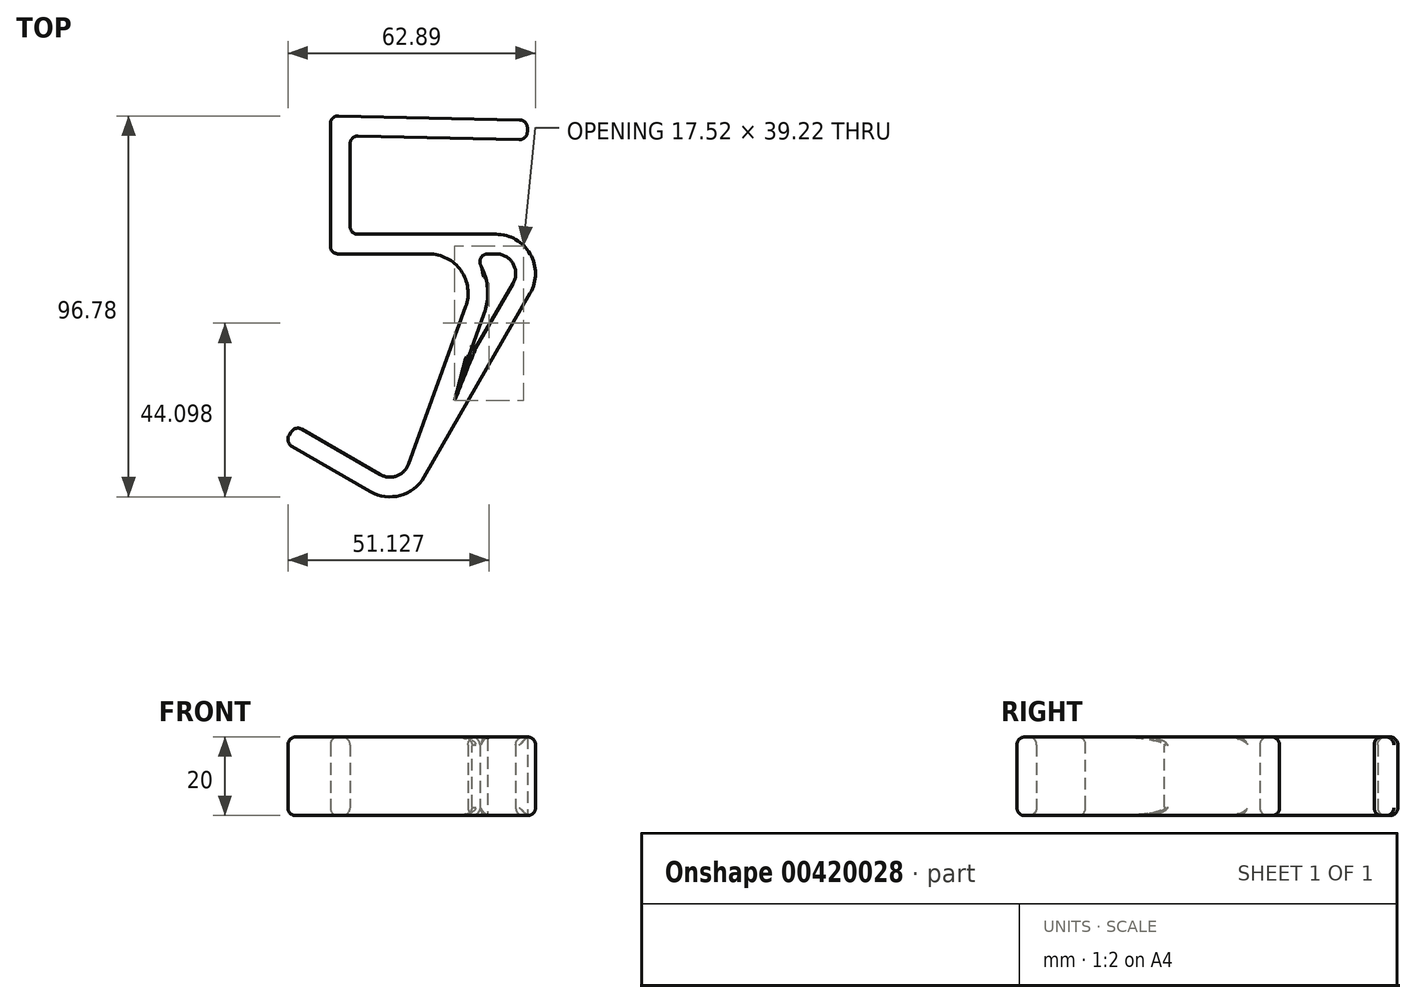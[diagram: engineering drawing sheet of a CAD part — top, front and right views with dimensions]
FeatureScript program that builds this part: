
annotation { "Feature Type Name" : "Feature", "Feature Type Description" : "" }
export const myFeature = defineFeature(function(context is Context, id is Id, definition is map)
    precondition{}
    {
        {
            var Q0;
            Q0=qCreatedBy(makeId("Top.planeOp"),FACE);
            var sketch = newSketch(context, id + "F0", { "sketchPlane" : qUnion([Q0])});
            skLineSegment(sketch, "E0.top", {"start": v(14.6, -12.5) * mm, "end": v(-22.5, -12.5) * mm});
            skLineSegment(sketch, "E0.right", {"start": v(-22.5, 12.5) * mm, "end": v(-22.5, -12.5) * mm});
            skPoint(sketch, "E0.middle", {"position": v(0, 0) * mm});
            skLineSegment(sketch, "E1", {"start": v(-22.5, 12.5) * mm, "end": v(22.5, 11.5) * mm});
            skLineSegment(sketch, "E2", {"start": v(6.9, -30.92) * mm, "end": v(-7.66, -70.92) * mm});
            skLineSegment(sketch, "E3", {"start": v(-14.86, -73.54) * mm, "end": v(-36.51, -61.04) * mm});
            skLineSegment(sketch, "E4.0", {"start": v(-27.5, 17.61) * mm, "end": v(22.61, 16.5) * mm});
            skLineSegment(sketch, "E4.1", {"start": v(-27.5, 17.61) * mm, "end": v(-27.5, -17.5) * mm});
            skLineSegment(sketch, "E4.2", {"start": v(-2.5, -17.5) * mm, "end": v(-27.5, -17.5) * mm});
            skPoint(sketch, "E5.visualSharp", {"position": v(-9.7, -76.52) * mm});
            skArc(sketch, "E5.filletArc", {"start": v(-14.86, -73.54) * mm, "mid": v(-10.65, -73.9) * mm, "end": v(-7.66, -70.92) * mm});
            skArc(sketch, "E6.filletArc", {"start": v(6.9, -30.92) * mm, "mid": v(5.7, -21.76) * mm, "end": v(-2.5, -17.5) * mm});
            skLineSegment(sketch, "E7.0", {"start": v(-17.36, -77.87) * mm, "end": v(-39.01, -65.37) * mm});
            skArc(sketch, "E7.1", {"start": v(-17.36, -77.87) * mm, "mid": v(-9.77, -78.87) * mm, "end": v(-3.7, -74.21) * mm});
            skLineSegment(sketch, "E7.2", {"start": v(11.6, -32.63) * mm, "end": v(6.59, -46.4) * mm});
            skArc(sketch, "E7.3", {"start": v(11.6, -32.63) * mm, "mid": v(12.23, -24.66) * mm, "end": v(8.68, -17.5) * mm});
            skLineSegment(sketch, "E8", {"start": v(-3.7, -74.21) * mm, "end": v(23.27, -27.5) * mm});
            skArc(sketch, "E9.filletArc", {"start": v(23.27, -27.5) * mm, "mid": v(23.27, -17.5) * mm, "end": v(14.6, -12.5) * mm});
            skLineSegment(sketch, "E10.0", {"start": v(14.6, -17.5) * mm, "end": v(-22.5, -17.5) * mm});
            skArc(sketch, "E10.1", {"start": v(18.94, -25) * mm, "mid": v(18.94, -20) * mm, "end": v(14.6, -17.5) * mm});
            skLineSegment(sketch, "E10.2", {"start": v(6.59, -46.4) * mm, "end": v(18.94, -25) * mm});
            skArc(sketch, "E11", {"start": v(8.68, -17.5) * mm, "mid": v(3.62, -13.8) * mm, "end": v(-2.5, -12.5) * mm, "construction": true});
            skLineSegment(sketch, "E12", {"start": v(22.61, 16.5) * mm, "end": v(22.5, 11.5) * mm});
            skLineSegment(sketch, "E13", {"start": v(-39.01, -65.37) * mm, "end": v(-36.51, -61.04) * mm});
            skSolve(sketch);
        }
        {
            var Q0;
            Q0=qSketchRegion(id+"F0",true);
            var Q1;
            Q1=makeQuery(id+"F0.imprint","IMPRINT",FACE,{"disambiguationData":[TD([[makeQuery(id+"F0.imprint","IMPRINT",EDGE,{"derivedFrom":sQuery(id+"F0.wireOp",EDGE,"E0.top")}),1.0]])]});
            extrude(context, id + "F1", {"entities" : qUnion([Q0, Q1]), "depth" : 20 * mm});
        }
        {
            var Q0;
            Q0=makeQuery(id+"F1.opExtrude","SWEPT_FACE",FACE,{"disambiguationData":[OSD([sQuery(id+"F0.wireOp",EDGE,"E4.1")])]});
            var Q1;
            Q1=makeQuery(id+"F1.opExtrude","SWEPT_FACE",FACE,{"disambiguationData":[OSD([sQuery(id+"F0.wireOp",EDGE,"E4.2"),sQuery(id+"F0.wireOp",EDGE,"E10.0")])]});
            var Q2;
            Q2=makeQuery(id+"F1.opExtrude","SWEPT_FACE",FACE,{"disambiguationData":[OSD([sQuery(id+"F0.wireOp",EDGE,"E4.0")])]});
            fillet(context, id + "F2", {"entities" : qUnion([Q0, Q1, Q2]), "radius" : 2 * mm, "tangentPropagation" : true, "allowEdgeOverflow" : false});
        }
        {
            var Q0;
            Q0=makeQuery(id+"F1.opExtrude","SWEPT_FACE",FACE,{"disambiguationData":[OSD([sQuery(id+"F0.wireOp",EDGE,"E8")])]});
            fillet(context, id + "F3", {"entities" : qUnion([Q0]), "radius" : 2 * mm, "tangentPropagation" : true, "allowEdgeOverflow" : false});
        }
        {
            var Q0;
            Q0=makeQuery(id+"F1.opExtrude","SWEPT_FACE",FACE,{"disambiguationData":[OSD([sQuery(id+"F0.wireOp",EDGE,"E1")])]});
            var Q1;
            Q1=makeQuery(id+"F1.opExtrude","SWEPT_FACE",FACE,{"disambiguationData":[OSD([sQuery(id+"F0.wireOp",EDGE,"E0.right")])]});
            fillet(context, id + "F4", {"entities" : qUnion([Q0, Q1]), "radius" : 2 * mm, "allowEdgeOverflow" : false});
        }
        {
            var Q0;
            Q0=makeQuery(id+"F1.opExtrude","SWEPT_FACE",FACE,{"disambiguationData":[OSD([sQuery(id+"F0.wireOp",EDGE,"E13")])]});
            fillet(context, id + "F5", {"entities" : qUnion([Q0]), "radius" : 2 * mm, "tangentPropagation" : true, "allowEdgeOverflow" : false});
        }
        {
            var Q0;
            Q0=makeQuery(id+"F1.opExtrude","SWEPT_FACE",FACE,{"disambiguationData":[OSD([sQuery(id+"F0.wireOp",EDGE,"E7.3")])]});
            var Q1;
            Q1=makeQuery(id+"F1.opExtrude","SWEPT_FACE",FACE,{"disambiguationData":[OSD([sQuery(id+"F0.wireOp",EDGE,"E7.2")])]});
            var Q2;
            Q2=makeQuery(id+"F1.opExtrude","SWEPT_FACE",FACE,{"disambiguationData":[OSD([sQuery(id+"F0.wireOp",EDGE,"E10.0")])]});
            var Q3;
            Q3=makeQuery(id+"F1.opExtrude","SWEPT_FACE",FACE,{"disambiguationData":[OSD([sQuery(id+"F0.wireOp",EDGE,"E10.1")])]});
            var Q4;
            Q4=makeQuery(id+"F1.opExtrude","SWEPT_FACE",FACE,{"disambiguationData":[OSD([sQuery(id+"F0.wireOp",EDGE,"E10.2")])]});
            fillet(context, id + "F6", {"entities" : qUnion([Q0, Q1, Q2, Q3, Q4]), "radius" : 0.5 * mm, "tangentPropagation" : true, "allowEdgeOverflow" : false});
        }
    });
